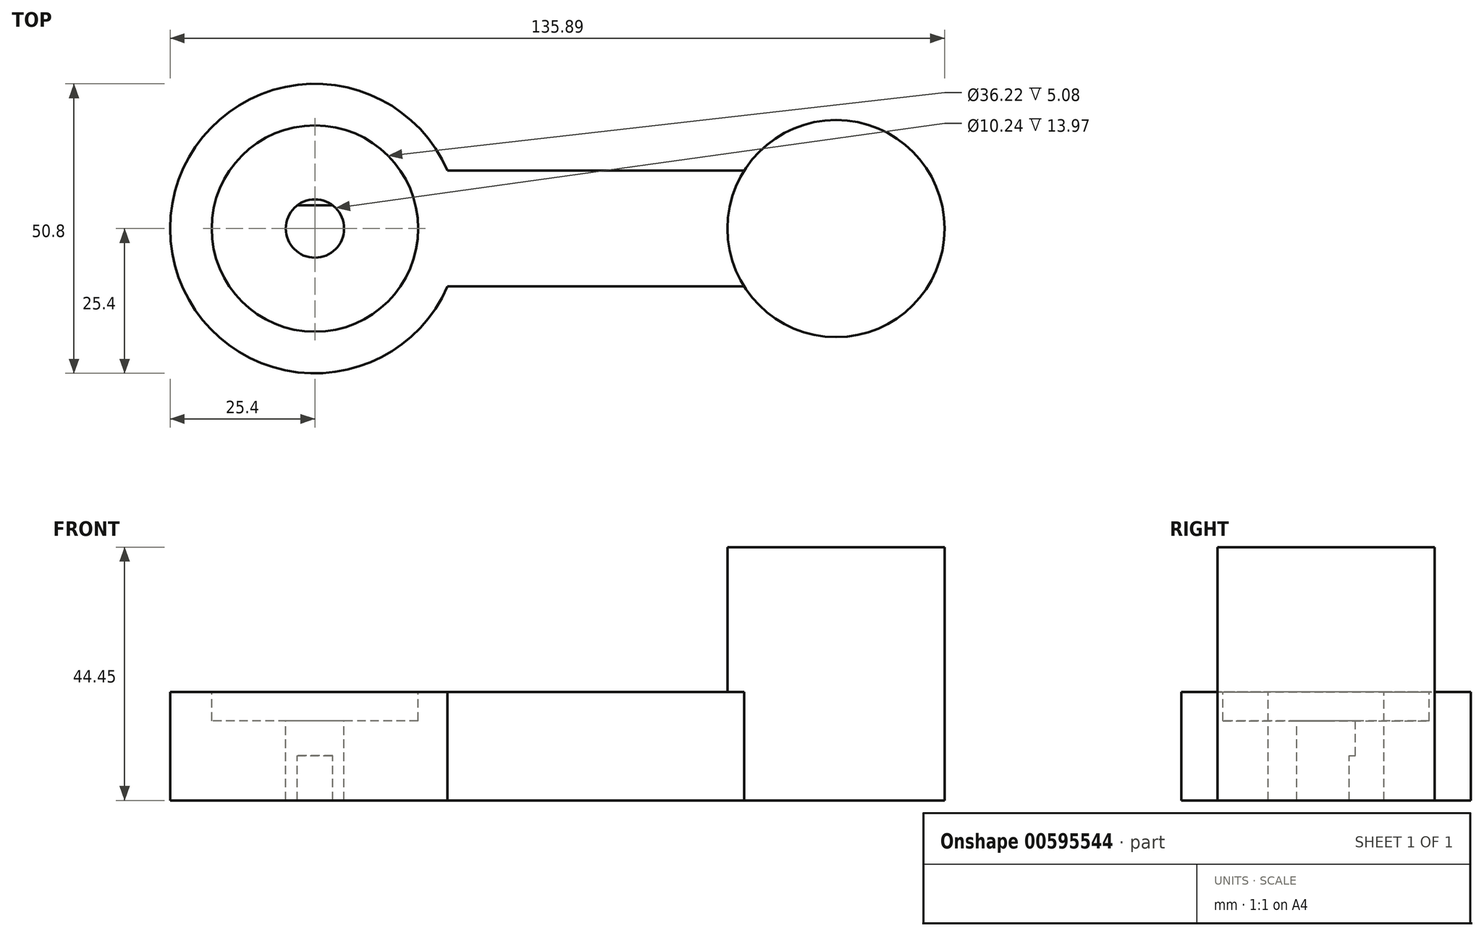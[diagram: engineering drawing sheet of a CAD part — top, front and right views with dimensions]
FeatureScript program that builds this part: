
annotation { "Feature Type Name" : "Feature", "Feature Type Description" : "" }
export const myFeature = defineFeature(function(context is Context, id is Id, definition is map)
    precondition{}
    {
        {
            var Q0;
            Q0=qCreatedBy(makeId("Top.planeOp"),FACE);
            var sketch = newSketch(context, id + "F0", { "sketchPlane" : qUnion([Q0])});
            skCircle(sketch, "E0", {"center": v(0, 0) * mm, "radius": 25.4 * mm});
            skCircle(sketch, "E1", {"center": v(0, 0) * mm, "radius": 18.11 * mm});
            skCircle(sketch, "E2", {"center": v(0, 0) * mm, "radius": 5.12 * mm});
            skLineSegment(sketch, "E3", {"start": v(-3.13, 4.05) * mm, "end": v(3.13, 4.05) * mm});
            skLineSegment(sketch, "E4", {"start": v(0, 0) * mm, "end": v(72.4, 0) * mm});
            skLineSegment(sketch, "E5", {"start": v(23.28, 10.16) * mm, "end": v(75.33, 10.16) * mm});
            skLineSegment(sketch, "E6", {"start": v(23.28, -10.16) * mm, "end": v(75.33, -10.16) * mm});
            skCircle(sketch, "E7", {"center": v(91.44, 0) * mm, "radius": 19.05 * mm});
            skPoint(sketch, "E8.orphan", {"position": v(91.44, 10.16) * mm});
            skPoint(sketch, "E9.orphan", {"position": v(91.44, -10.16) * mm});
            skSolve(sketch);
        }
        {
            var Q0;
            Q0=makeQuery(id+"F0.imprint","IMPRINT",FACE,{"disambiguationData":[TD([[makeQuery(id+"F0.imprint","IMPRINT",EDGE,{"derivedFrom":sQuery(id+"F0.wireOp",EDGE,"E1")}),-1.0]])]});
            var Q1;
            Q1=makeQuery(id+"F0.imprint","IMPRINT",FACE,{"disambiguationData":[TD([[makeQuery(id+"F0.imprint","IMPRINT",EDGE,{"derivedFrom":sQuery(id+"F0.wireOp",EDGE,"E1")}),1.0]])]});
            var Q2;
            {var subQ0=sQuery(id+"F0.wireOp",EDGE,"E3");Q2=makeQuery(id+"F0.imprint","IMPRINT",FACE,{"disambiguationData":[TD([[makeQuery(id+"F0.imprint","IMPRINT",EDGE,{"derivedFrom":subQ0}),-1.0]])]});}
            var Q3;
            {var subQ0=sQuery(id+"F0.wireOp",EDGE,"E3");Q3=makeQuery(id+"F0.imprint","IMPRINT",FACE,{"disambiguationData":[TD([[makeQuery(id+"F0.imprint","IMPRINT",EDGE,{"derivedFrom":subQ0}),1.0]])]});}
            var Q4;
            {var subQ0=sQuery(id+"F0.wireOp",EDGE,"E6");Q4=makeQuery(id+"F0.imprint","IMPRINT",FACE,{"disambiguationData":[TD([[makeQuery(id+"F0.imprint","IMPRINT",EDGE,{"derivedFrom":subQ0}),1.0]])]});}
            var Q5;
            {var subQ0=sQuery(id+"F0.wireOp",EDGE,"E5");Q5=makeQuery(id+"F0.imprint","IMPRINT",FACE,{"disambiguationData":[TD([[makeQuery(id+"F0.imprint","IMPRINT",EDGE,{"derivedFrom":subQ0}),-1.0]])]});}
            var Q6;
            {var subQ0=sQuery(id+"F0.wireOp",EDGE,"E7");var subQ1=makeQuery(id+"F0.imprint","INTERSECT",VERTEX,{"derivedFrom":[sQuery(id+"F0.wireOp",EDGE,"E4"),subQ0]});Q6=makeQuery(id+"F0.imprint","IMPRINT",FACE,{"disambiguationData":[TD([[makeQuery(id+"F0.imprint","IMPRINT",EDGE,{"disambiguationData":[TD([[subQ1,1.0]])],"derivedFrom":subQ0}),1.0]])]});}
            extrude(context, id + "F1", {"entities" : qUnion([Q0, Q1, Q2, Q3, Q4, Q5, Q6]), "oppositeDirection" : true, "depth" : 19.05 * mm, "offsetDistance" : 25.4 * mm});
        }
        {
            var Q0;
            {var subQ0=sQuery(id+"F0.wireOp",EDGE,"E7");var subQ1=makeQuery(id+"F0.imprint","INTERSECT",VERTEX,{"derivedFrom":[sQuery(id+"F0.wireOp",EDGE,"E4"),subQ0]});Q0=makeQuery(id+"F0.imprint","IMPRINT",FACE,{"disambiguationData":[TD([[makeQuery(id+"F0.imprint","IMPRINT",EDGE,{"disambiguationData":[TD([[subQ1,1.0]])],"derivedFrom":subQ0}),1.0]])]});}
            extrude(context, id + "F2", {"entities" : qUnion([Q0]), "operationType" : NewBodyOperationType.ADD, "depth" : 25.4 * mm, "offsetDistance" : 25.4 * mm});
        }
        {
            var Q0;
            Q0=makeQuery(id+"F0.imprint","IMPRINT",FACE,{"disambiguationData":[TD([[makeQuery(id+"F0.imprint","IMPRINT",EDGE,{"derivedFrom":sQuery(id+"F0.wireOp",EDGE,"E1")}),1.0]])]});
            var Q1;
            {var subQ0=sQuery(id+"F0.wireOp",EDGE,"E3");Q1=makeQuery(id+"F0.imprint","IMPRINT",FACE,{"disambiguationData":[TD([[makeQuery(id+"F0.imprint","IMPRINT",EDGE,{"derivedFrom":subQ0}),-1.0]])]});}
            var Q2;
            {var subQ0=sQuery(id+"F0.wireOp",EDGE,"E3");Q2=makeQuery(id+"F0.imprint","IMPRINT",FACE,{"disambiguationData":[TD([[makeQuery(id+"F0.imprint","IMPRINT",EDGE,{"derivedFrom":subQ0}),1.0]])]});}
            extrude(context, id + "F3", {"entities" : qUnion([Q0, Q1, Q2]), "operationType" : NewBodyOperationType.REMOVE, "oppositeDirection" : true, "depth" : 5.08 * mm, "offsetDistance" : 25.4 * mm});
        }
        {
            var Q0;
            {var subQ0=sQuery(id+"F0.wireOp",EDGE,"E3");Q0=makeQuery(id+"F0.imprint","IMPRINT",FACE,{"disambiguationData":[TD([[makeQuery(id+"F0.imprint","IMPRINT",EDGE,{"derivedFrom":subQ0}),-1.0]])]});}
            var Q1;
            {var subQ0=sQuery(id+"F0.wireOp",EDGE,"E3");Q1=makeQuery(id+"F0.imprint","IMPRINT",FACE,{"disambiguationData":[TD([[makeQuery(id+"F0.imprint","IMPRINT",EDGE,{"derivedFrom":subQ0}),1.0]])]});}
            extrude(context, id + "F4", {"entities" : qUnion([Q0, Q1]), "operationType" : NewBodyOperationType.REMOVE, "oppositeDirection" : true, "depth" : 11.18 * mm, "offsetDistance" : 25.4 * mm});
        }
        {
            var Q0;
            {var subQ0=sQuery(id+"F0.wireOp",EDGE,"E3");Q0=makeQuery(id+"F0.imprint","IMPRINT",FACE,{"disambiguationData":[TD([[makeQuery(id+"F0.imprint","IMPRINT",EDGE,{"derivedFrom":subQ0}),-1.0]])]});}
            extrude(context, id + "F5", {"entities" : qUnion([Q0]), "operationType" : NewBodyOperationType.REMOVE, "oppositeDirection" : true, "depth" : 20.32 * mm, "offsetDistance" : 25.4 * mm});
        }
    });
